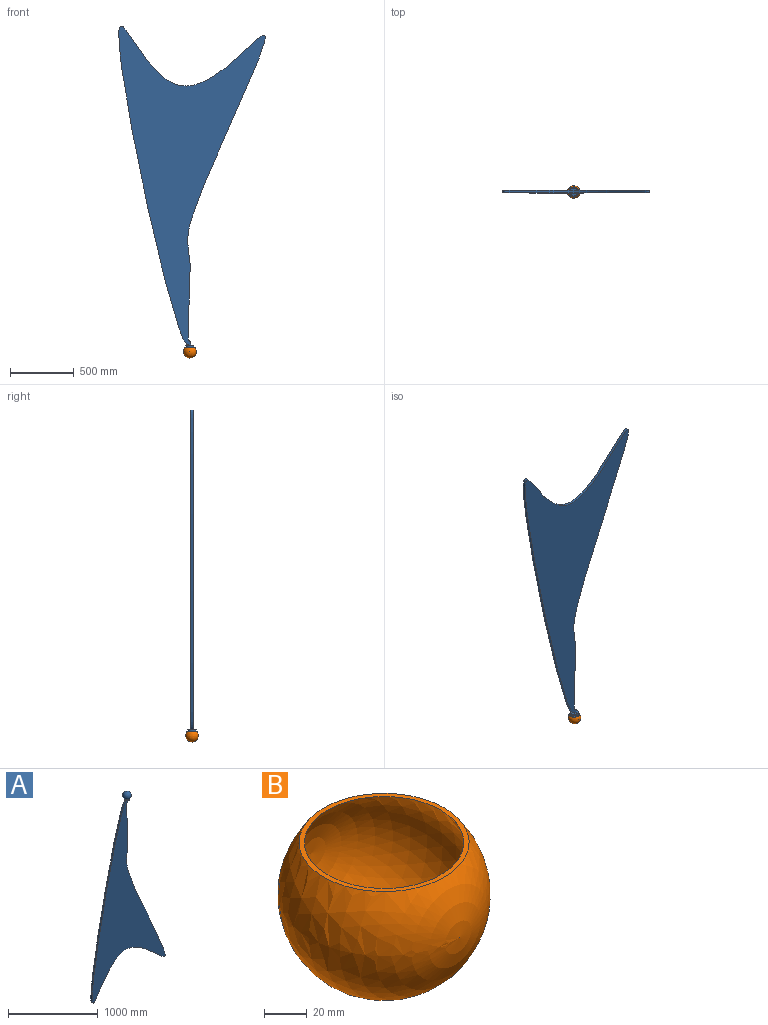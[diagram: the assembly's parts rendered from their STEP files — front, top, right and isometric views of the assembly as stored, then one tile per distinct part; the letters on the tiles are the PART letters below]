
ASSEMBLY  parts=2 mates=1
PART A: 7 faces, bbox 1489.2x96x2776.4 mm
  f0: extruded ~2498.35x1145.34mm, area 128758.6mm2, adj f1,f2,f3
  f1: plane 2699.2x1489.2mm, normal (0,1,0), area 1019624.8mm2, adj f0,f3
  f2: plane 2699.2x1489.2mm, normal (0,-1,0), area 1019624.8mm2, adj f0,f3
  f3: plane 63.63x63.63mm, normal (0,0,-1), area 2836.7mm2, adj f0,f1,f2,f4
  f4: cylinder r=31.82mm len=63.63mm, axis (0,0,-1), area 2998.7mm2, adj f3,f5
  f5: plane 63.63x63.63mm, normal (0,0,1), area 89.6mm2, adj f4,f6
  f6: sphere r=48mm, area 25434.7mm2, adj f5
PART B: 3 faces, bbox 100x100x100 mm
  f0: plane 80x80mm, normal (0,0,1), area 615.8mm2, adj f1,f2
  f1: sphere r=50mm, area 25133.5mm2, adj f0
  f2: sphere r=48mm, area 23524.9mm2, adj f0
PLACE A rot(axis=(1,0,0),180deg) t=(0,0,0)mm
PLACE B at identity
MATE ball A.f4 <-> B.f1  axis (0,0,-1) through (0,0,0)mm
